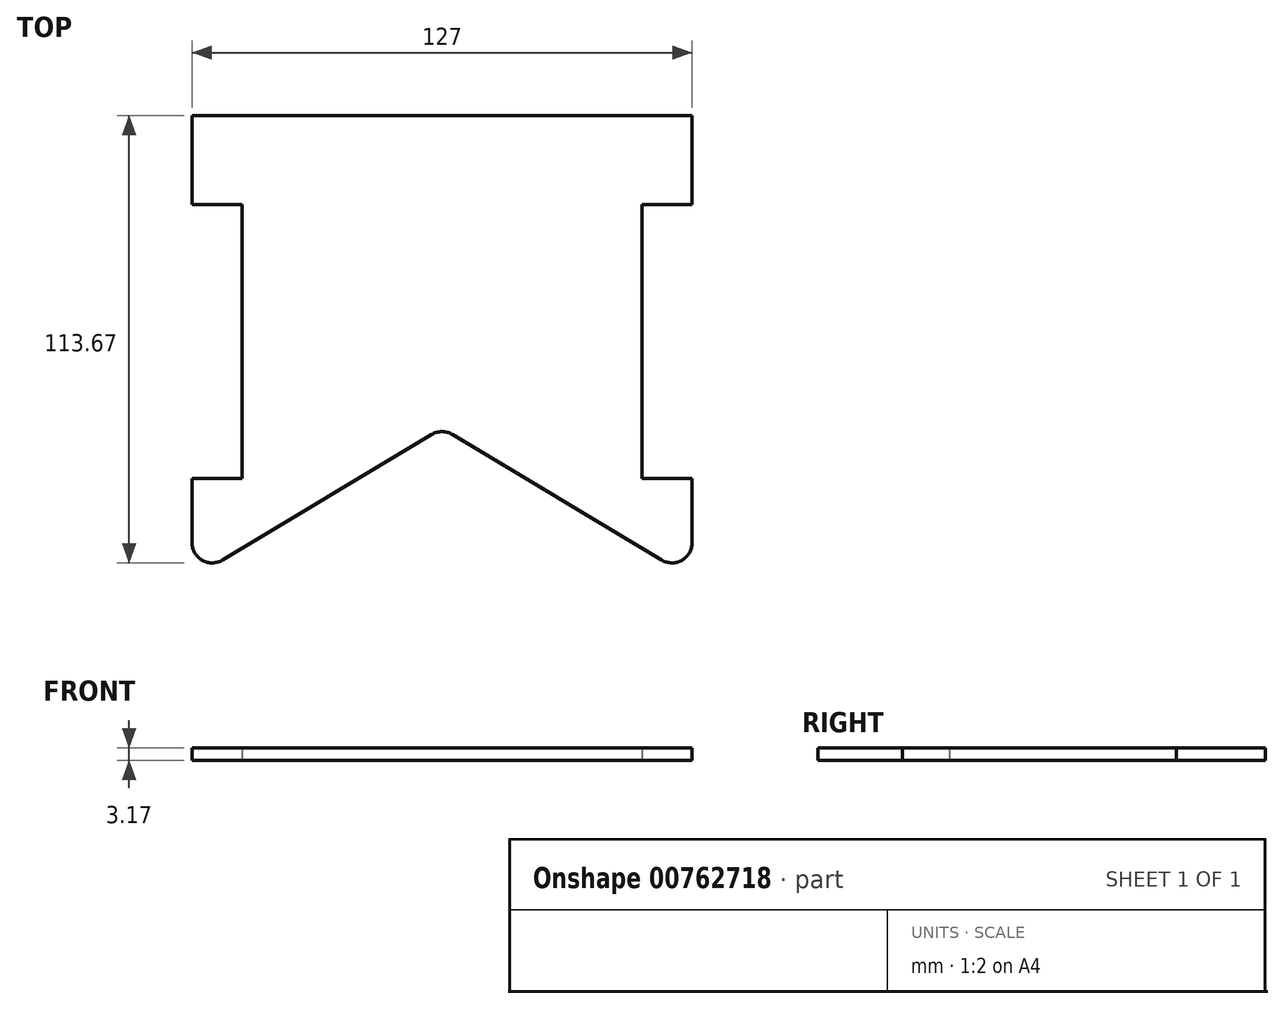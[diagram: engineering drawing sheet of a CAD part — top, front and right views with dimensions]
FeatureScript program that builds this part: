
annotation { "Feature Type Name" : "Feature", "Feature Type Description" : "" }
export const myFeature = defineFeature(function(context is Context, id is Id, definition is map)
    precondition{}
    {
        {
            var Q0;
            Q0=qCreatedBy(makeId("Top.planeOp"),FACE);
            var sketch = newSketch(context, id + "F0", { "sketchPlane" : qUnion([Q0])});
            skLineSegment(sketch, "E0", {"start": v(-50.8, 24.59) * mm, "end": v(-50.8, -32.28) * mm});
            skLineSegment(sketch, "E1", {"start": v(-63.5, -70.38) * mm, "end": v(0, -32.28) * mm});
            skLineSegment(sketch, "E2.MirrorCS", {"start": v(50.8, 24.59) * mm, "end": v(50.8, -32.28) * mm});
            skLineSegment(sketch, "E3.MirrorCS", {"start": v(63.5, -70.38) * mm, "end": v(0, -32.28) * mm});
            skLineSegment(sketch, "E4", {"start": v(-50.8, 24.59) * mm, "end": v(-50.8, 47.18) * mm});
            skLineSegment(sketch, "E5", {"start": v(50.8, 24.59) * mm, "end": v(50.8, 47.18) * mm});
            skLineSegment(sketch, "E6", {"start": v(-50.8, 47.18) * mm, "end": v(0, 47.18) * mm});
            skLineSegment(sketch, "E7", {"start": v(0, 47.18) * mm, "end": v(50.8, 47.18) * mm});
            skLineSegment(sketch, "E8", {"start": v(-63.5, -70.38) * mm, "end": v(-63.5, -44.98) * mm});
            skLineSegment(sketch, "E9", {"start": v(63.5, -70.38) * mm, "end": v(63.5, -44.98) * mm});
            skLineSegment(sketch, "E10", {"start": v(-63.5, -44.98) * mm, "end": v(-50.8, -44.98) * mm});
            skLineSegment(sketch, "E11", {"start": v(-50.8, -44.98) * mm, "end": v(-50.8, 24.59) * mm});
            skLineSegment(sketch, "E12", {"start": v(63.5, -44.98) * mm, "end": v(50.8, -44.98) * mm});
            skLineSegment(sketch, "E13", {"start": v(50.8, -44.98) * mm, "end": v(50.8, 24.59) * mm});
            skLineSegment(sketch, "E14", {"start": v(-50.8, 24.59) * mm, "end": v(-63.5, 24.59) * mm});
            skLineSegment(sketch, "E15", {"start": v(50.8, 24.59) * mm, "end": v(63.5, 24.59) * mm});
            skLineSegment(sketch, "E16", {"start": v(63.5, 24.59) * mm, "end": v(63.5, 47.18) * mm});
            skLineSegment(sketch, "E17", {"start": v(63.5, 47.18) * mm, "end": v(50.8, 47.18) * mm});
            skLineSegment(sketch, "E18", {"start": v(-63.5, 24.59) * mm, "end": v(-63.5, 47.18) * mm});
            skLineSegment(sketch, "E19", {"start": v(-63.5, 47.18) * mm, "end": v(-50.8, 47.18) * mm});
            skSolve(sketch);
        }
        {
            var Q0;
            Q0=makeQuery(id+"F0.imprint","IMPRINT",FACE,{"disambiguationData":[TD([[makeQuery(id+"F0.imprint","IMPRINT",EDGE,{"derivedFrom":sQuery(id+"F0.wireOp",EDGE,"NGOt6KKF-8IpK-x8wM-DtWD-dQP0RAvZBKWF")}),1.0]])]});
            var Q1;
            Q1=makeQuery(id+"F0.imprint","IMPRINT",FACE,{"disambiguationData":[TD([[makeQuery(id+"F0.imprint","IMPRINT",EDGE,{"derivedFrom":sQuery(id+"F0.wireOp",EDGE,"E1")}),1.0]])]});
            var Q2;
            Q2=makeQuery(id+"F0.imprint","IMPRINT",FACE,{"disambiguationData":[TD([[makeQuery(id+"F0.imprint","IMPRINT",EDGE,{"derivedFrom":sQuery(id+"F0.wireOp",EDGE,"E4")}),1.0]])]});
            var Q3;
            Q3=makeQuery(id+"F0.imprint","IMPRINT",FACE,{"disambiguationData":[TD([[makeQuery(id+"F0.imprint","IMPRINT",EDGE,{"derivedFrom":sQuery(id+"F0.wireOp",EDGE,"E5")}),-1.0]])]});
            extrude(context, id + "F1", {"entities" : qUnion([Q0, Q1, Q2, Q3]), "depth" : 3.17 * mm, "offsetDistance" : 25.4 * mm});
        }
        {
            var Q0;
            Q0=makeQuery(id+"F1.opExtrude","SWEPT_EDGE",EDGE,{"disambiguationData":[OSD([sQuery(id+"F0.wireOp",EDGE,"MHhSgwDd-k8az-dhf2-bJY8-4wMcgRs5HjQh"),sQuery(id+"F0.wireOp",EDGE,"E1")])]});
            fillet(context, id + "F2", {"entities" : qUnion([Q0]), "radius" : 5.08 * mm, "tangentPropagation" : true, "allowEdgeOverflow" : false});
        }
        {
            var Q0;
            Q0=makeQuery(id+"F1.opExtrude","SWEPT_EDGE",EDGE,{"disambiguationData":[OSD([sQuery(id+"F0.wireOp",EDGE,"E3.MirrorCS"),sQuery(id+"F0.wireOp",EDGE,"E9")])]});
            fillet(context, id + "F3", {"entities" : qUnion([Q0]), "radius" : 5.08 * mm, "tangentPropagation" : true, "allowEdgeOverflow" : false});
        }
    });
